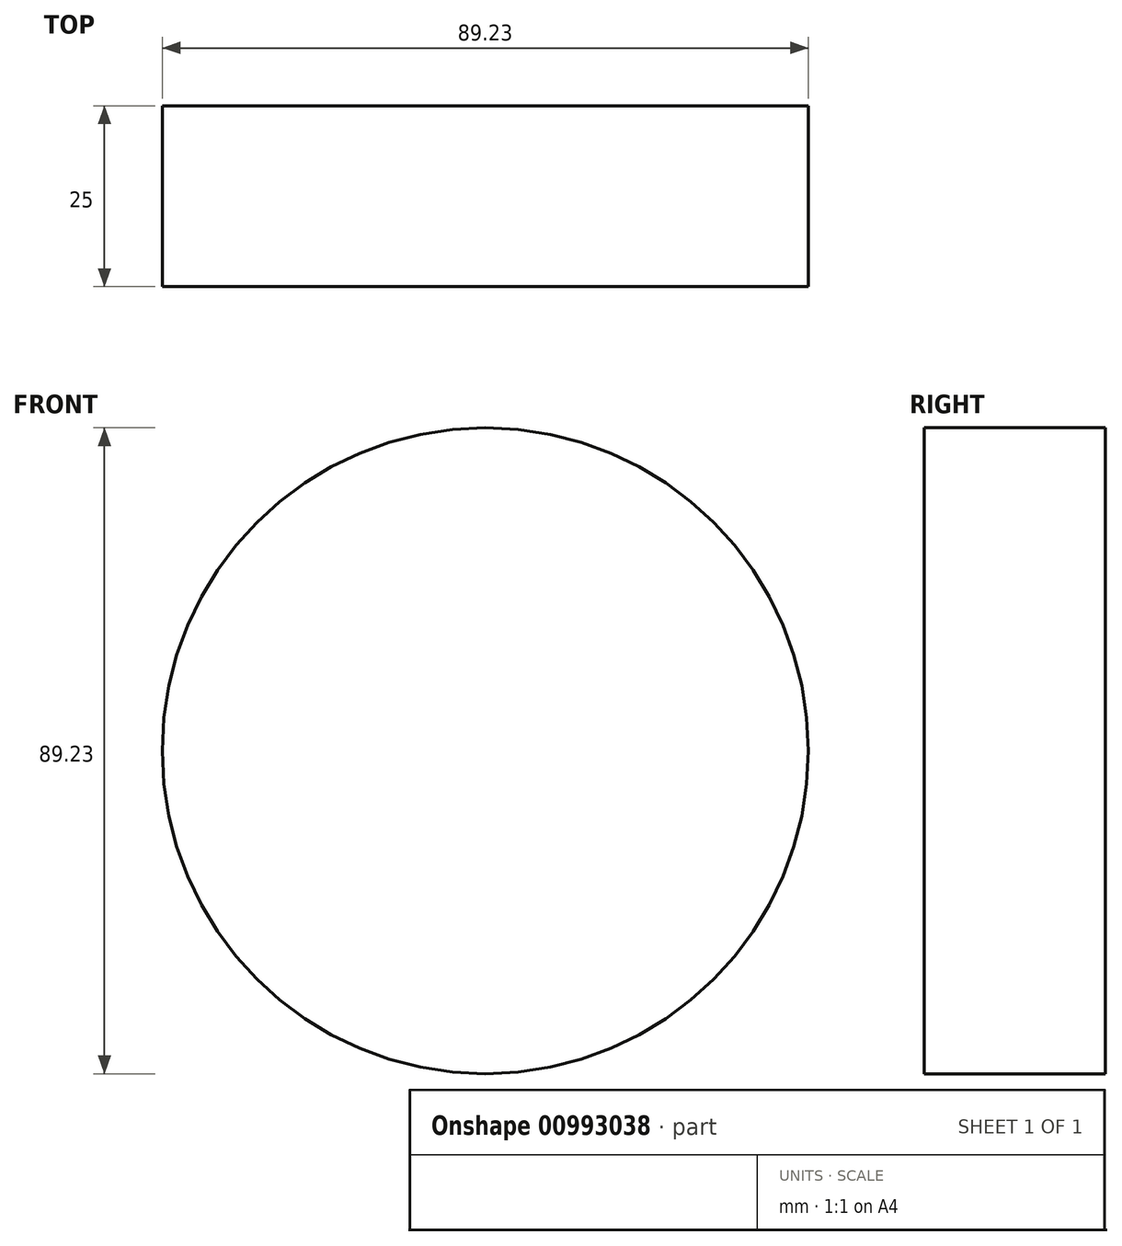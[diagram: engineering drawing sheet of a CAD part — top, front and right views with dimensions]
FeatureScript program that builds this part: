
annotation { "Feature Type Name" : "Feature", "Feature Type Description" : "" }
export const myFeature = defineFeature(function(context is Context, id is Id, definition is map)
    precondition{}
    {
        {
            var Q0;
            Q0=qCreatedBy(makeId("Front.planeOp"),FACE);
            var sketch = newSketch(context, id + "F0", { "sketchPlane" : qUnion([Q0])});
            skCircle(sketch, "E0", {"center": v(-141.53, -44.03) * mm, "radius": 44.62 * mm});
            skSolve(sketch);
        }
        {
            var Q0;
            Q0=makeQuery(id+"F0.imprint","IMPRINT",FACE,{"disambiguationData":[TD([[makeQuery(id+"F0.imprint","IMPRINT",EDGE,{"derivedFrom":sQuery(id+"F0.wireOp",EDGE,"E0")}),1.0]])]});
            extrude(context, id + "F1", {"entities" : qUnion([Q0]), "depth" : 25 * mm, "offsetDistance" : 25 * mm});
        }
    });
